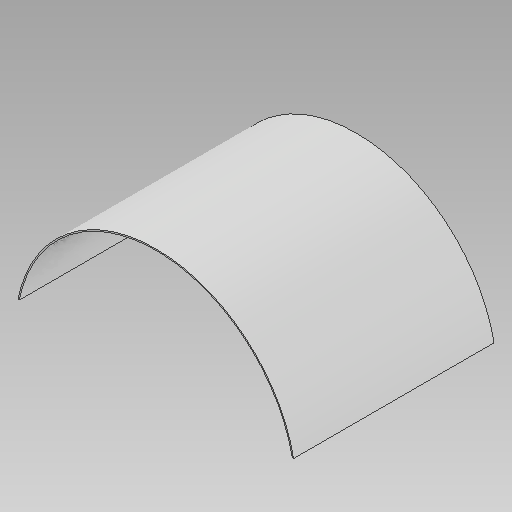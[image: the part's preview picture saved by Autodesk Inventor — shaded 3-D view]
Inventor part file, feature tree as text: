
AUTODESK INVENTOR PART (.ipt)
format: ipt  version: 2021 (Build 250183000, 183)  size: 117,248 bytes
history: native  units: mm
features: extrude x1, sketch x1
ambient origin geometry x8: Origin, YZ Plane, XZ Plane, XY Plane, X Axis, Y Axis, Z Axis, Center Point
bodies: Body1 (feature_tree)
feature tree (2):
  extrude  "shell"  Depth=10.0mm
  sketch  "Sketch2"  dims[d12=2200.0mm d13=900.0mm d14=1600.0mm d15=0.0mm d16=0.0mm d17=0.0mm d18=0.0mm d19=0.0mm d20=0.0mm d21=0.0mm d23=10.0mm]
